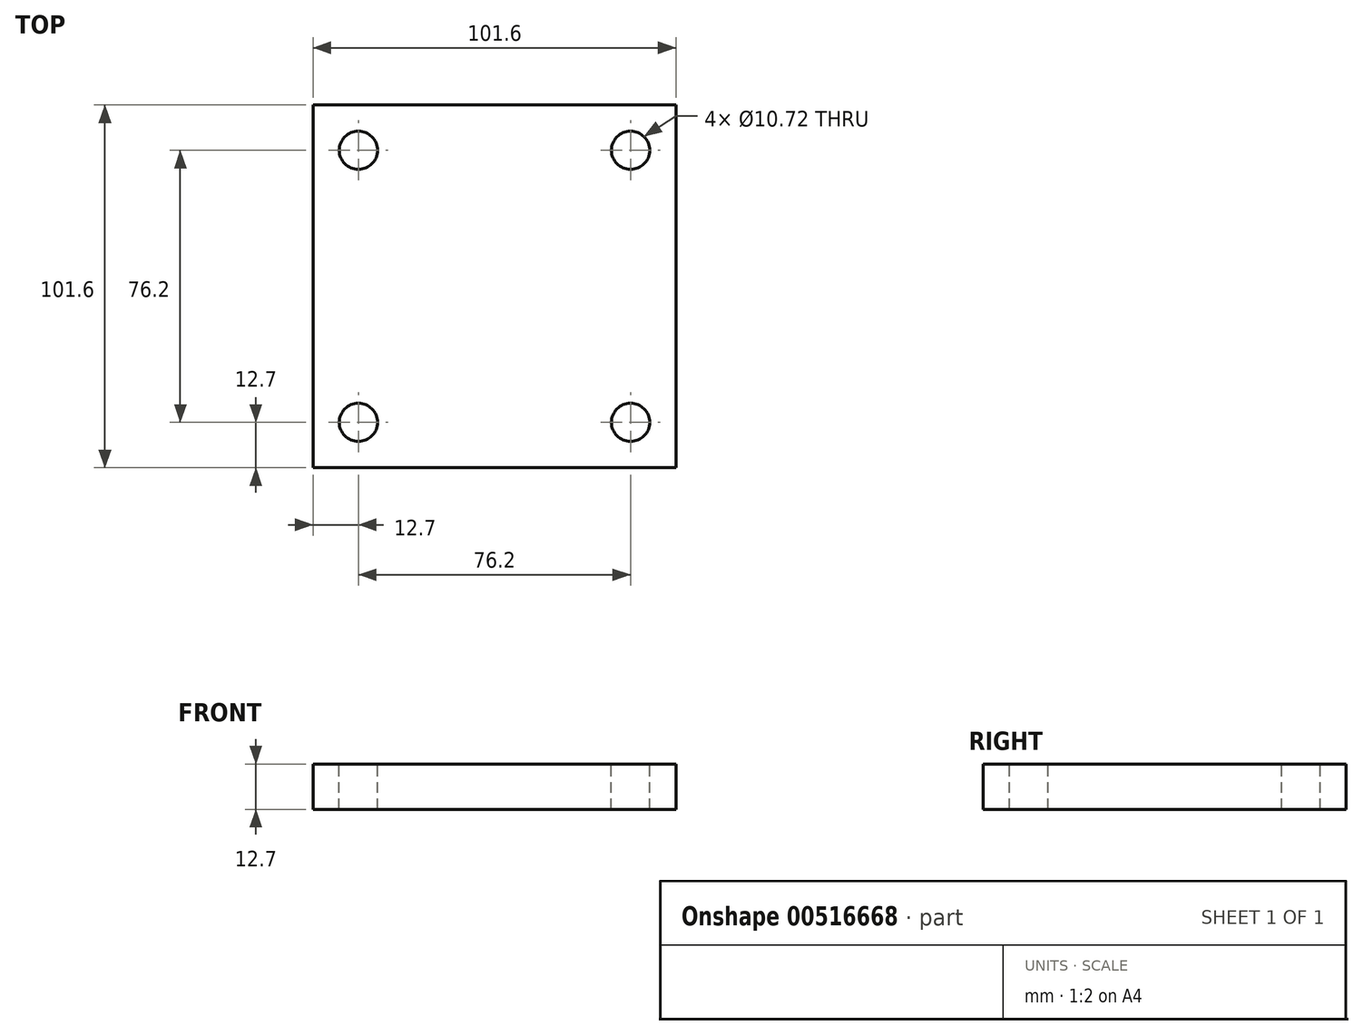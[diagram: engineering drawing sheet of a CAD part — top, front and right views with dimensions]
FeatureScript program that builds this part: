
annotation { "Feature Type Name" : "Feature", "Feature Type Description" : "" }
export const myFeature = defineFeature(function(context is Context, id is Id, definition is map)
    precondition{}
    {
        {
            var Q0;
            Q0=qCreatedBy(makeId("Top.planeOp"),FACE);
            var sketch = newSketch(context, id + "F0", { "sketchPlane" : qUnion([Q0])});
            skLineSegment(sketch, "E0.bottom", {"start": v(50.8, 50.8) * mm, "end": v(-50.8, 50.8) * mm});
            skLineSegment(sketch, "E0.top", {"start": v(50.8, -50.8) * mm, "end": v(-50.8, -50.8) * mm});
            skLineSegment(sketch, "E0.left", {"start": v(50.8, 50.8) * mm, "end": v(50.8, -50.8) * mm});
            skLineSegment(sketch, "E0.right", {"start": v(-50.8, 50.8) * mm, "end": v(-50.8, -50.8) * mm});
            skPoint(sketch, "E0.middle", {"position": v(0, 0) * mm});
            skSolve(sketch);
        }
        {
            var Q0;
            Q0=makeQuery(id+"F0.imprint","IMPRINT",FACE,{"disambiguationData":[TD([[makeQuery(id+"F0.imprint","IMPRINT",EDGE,{"derivedFrom":sQuery(id+"F0.wireOp",EDGE,"E0.bottom")}),1.0]])]});
            extrude(context, id + "F1", {"entities" : qUnion([Q0]), "endBound" : BoundingType.SYMMETRIC, "depth" : 12.7 * mm, "offsetDistance" : 25.4 * mm});
        }
        {
            var Q0;
            Q0=makeQuery(id+"F1.opExtrude","CAP_FACE",FACE,{"disambiguationData":[OSD([sQuery(id+"F0.wireOp",EDGE,"E0.bottom"),sQuery(id+"F0.wireOp",EDGE,"E0.top"),sQuery(id+"F0.wireOp",EDGE,"E0.left"),sQuery(id+"F0.wireOp",EDGE,"E0.right")])],"isStart":false});
            var sketch = newSketch(context, id + "F2", { "sketchPlane" : qUnion([Q0])});
            skPoint(sketch, "E1", {"position": v(-38.1, 38.1) * mm});
            skPoint(sketch, "E2", {"position": v(-38.1, -38.1) * mm});
            skPoint(sketch, "E3", {"position": v(38.1, -38.1) * mm});
            skPoint(sketch, "E4", {"position": v(38.1, 38.1) * mm});
            skSolve(sketch);
        }
        {
            var Q0;
            Q0=sQuery(id+"F2.wireOp",VERTEX,"E1");
            var Q1;
            Q1=sQuery(id+"F2.wireOp",VERTEX,"E4");
            var Q2;
            Q2=sQuery(id+"F2.wireOp",VERTEX,"E3");
            var Q3;
            Q3=sQuery(id+"F2.wireOp",VERTEX,"E2");
            var Q4;
            Q4=makeQuery(id+"F1.opExtrude","SWEPT_BODY",BODY,{"disambiguationData":[OSD([sQuery(id+"F0.wireOp",EDGE,"E0.bottom"),sQuery(id+"F0.wireOp",EDGE,"E0.top"),sQuery(id+"F0.wireOp",EDGE,"E0.left"),sQuery(id+"F0.wireOp",EDGE,"E0.right")])]});
            hole(context, id + "F3", {"style" : HoleStyle.SIMPLE, "endStyle" : HoleEndStyle.THROUGH, "standardTappedOrClearance" : lookupTablePath({ "standard" : "ANSI", "engagement" : "75%", "pitch" : "13 tpi", "size" : "1/2", "type" : "Tapped" }), "standardBlindInLast" : lookupTablePath({ "standard" : "ANSI", "engagement" : "75%", "pitch" : "13 tpi", "size" : "1/2", "type" : "Tapped" }), "holeDiameter" : 10.72 * mm, "showTappedDepth" : true, "isTappedThrough" : true, "tappedDepth" : 47.62 * mm, "tapClearance" : 3, "startFromSketch" : true, "locations" : qUnion([Q0, Q1, Q2, Q3]), "scope" : qUnion([Q4]), "majorDiameter" : 12.7 * mm});
        }
    });
